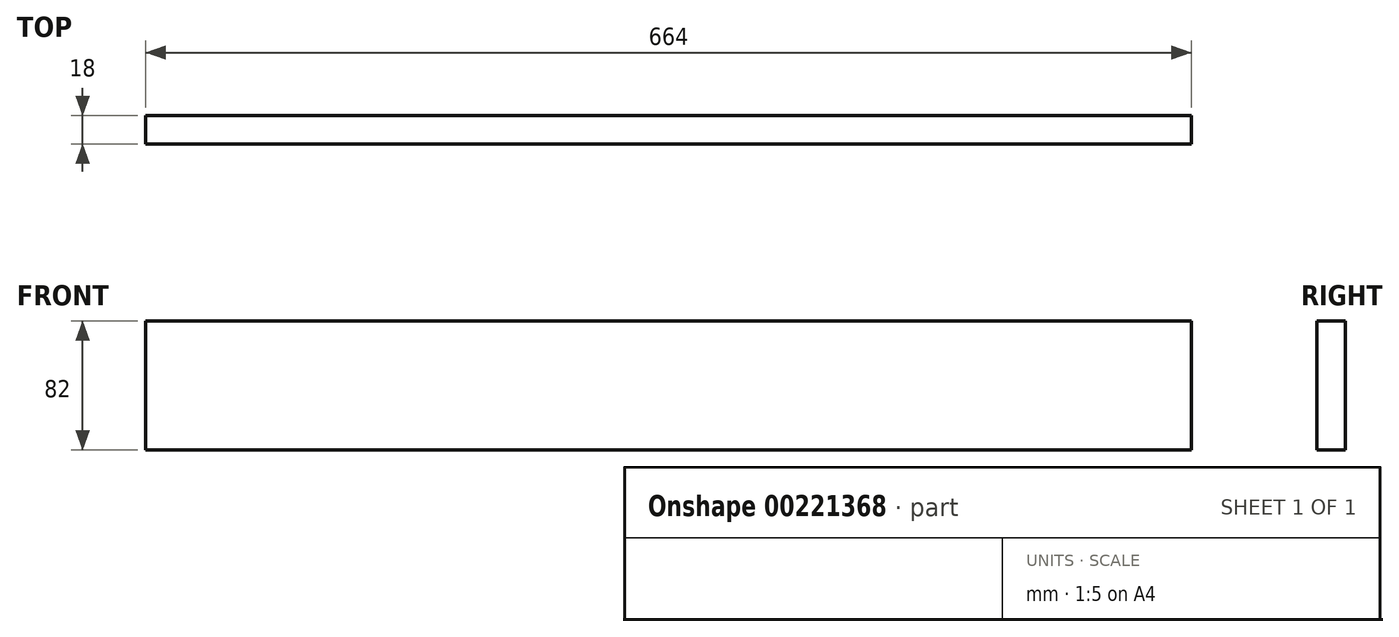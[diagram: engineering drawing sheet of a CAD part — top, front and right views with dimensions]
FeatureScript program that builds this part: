
annotation { "Feature Type Name" : "Feature", "Feature Type Description" : "" }
export const myFeature = defineFeature(function(context is Context, id is Id, definition is map)
    precondition{}
    {
        {
            var Q0;
            Q0=qCreatedBy(makeId("Front.planeOp"),FACE);
            var sketch = newSketch(context, id + "F0", { "sketchPlane" : qUnion([Q0])});
            skLineSegment(sketch, "E0.bottom", {"start": v(332, -41) * mm, "end": v(-332, -41) * mm});
            skLineSegment(sketch, "E0.top", {"start": v(332, 41) * mm, "end": v(-332, 41) * mm});
            skLineSegment(sketch, "E0.left", {"start": v(332, -41) * mm, "end": v(332, 41) * mm});
            skLineSegment(sketch, "E0.right", {"start": v(-332, -41) * mm, "end": v(-332, 41) * mm});
            skPoint(sketch, "E0.middle", {"position": v(0, 0) * mm});
            skSolve(sketch);
        }
        {
            var Q0;
            Q0 = qSketchRegion(id + "F0", true);
            extrude(context, id + "F1", {"entities" : qUnion([Q0]), "depth" : 18 * mm});
        }
    });
